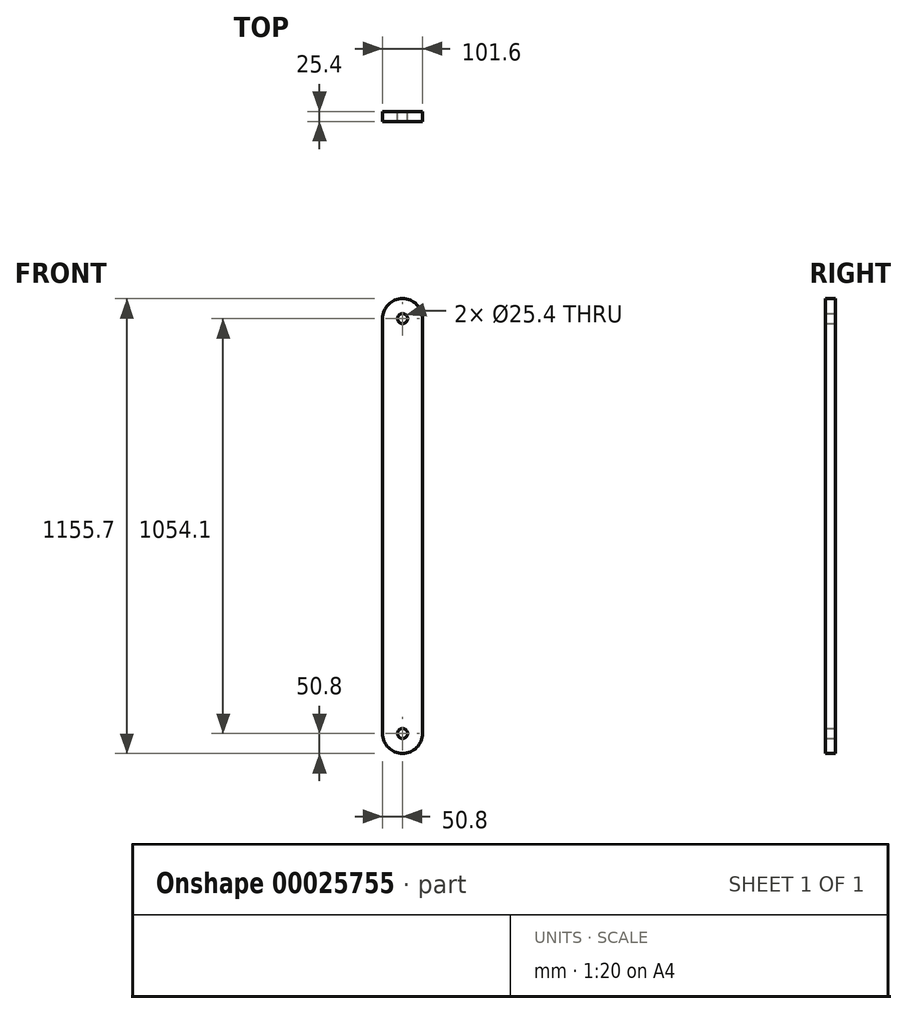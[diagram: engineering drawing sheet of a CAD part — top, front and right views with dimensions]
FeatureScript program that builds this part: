
annotation { "Feature Type Name" : "Feature", "Feature Type Description" : "" }
export const myFeature = defineFeature(function(context is Context, id is Id, definition is map)
    precondition{}
    {
        {
            var Q0;
            Q0=qCreatedBy(makeId("Front.planeOp"),FACE);
            var sketch = newSketch(context, id + "F0", { "sketchPlane" : qUnion([Q0])});
            skLineSegment(sketch, "E0", {"start": v(0, 0) * mm, "end": v(0, 1054.1) * mm});
            skLineSegment(sketch, "E1", {"start": v(-101.6, 0) * mm, "end": v(-101.6, 1054.1) * mm});
            skArc(sketch, "E2", {"start": v(0, 1054.1) * mm, "mid": v(-50.8, 1104.9) * mm, "end": v(-101.6, 1054.1) * mm});
            skArc(sketch, "E3", {"start": v(-101.6, 0) * mm, "mid": v(-50.8, -50.8) * mm, "end": v(0, 0) * mm});
            skCircle(sketch, "E4", {"center": v(-50.8, 1054.1) * mm, "radius": 12.7 * mm});
            skCircle(sketch, "E5", {"center": v(-50.8, 0) * mm, "radius": 12.7 * mm});
            skSolve(sketch);
        }
        {
            var Q0;
            Q0 = qSketchRegion(id + "F0", true);
            extrude(context, id + "F1", {"entities" : qUnion([Q0]), "depth" : 25.4 * mm});
        }
    });
